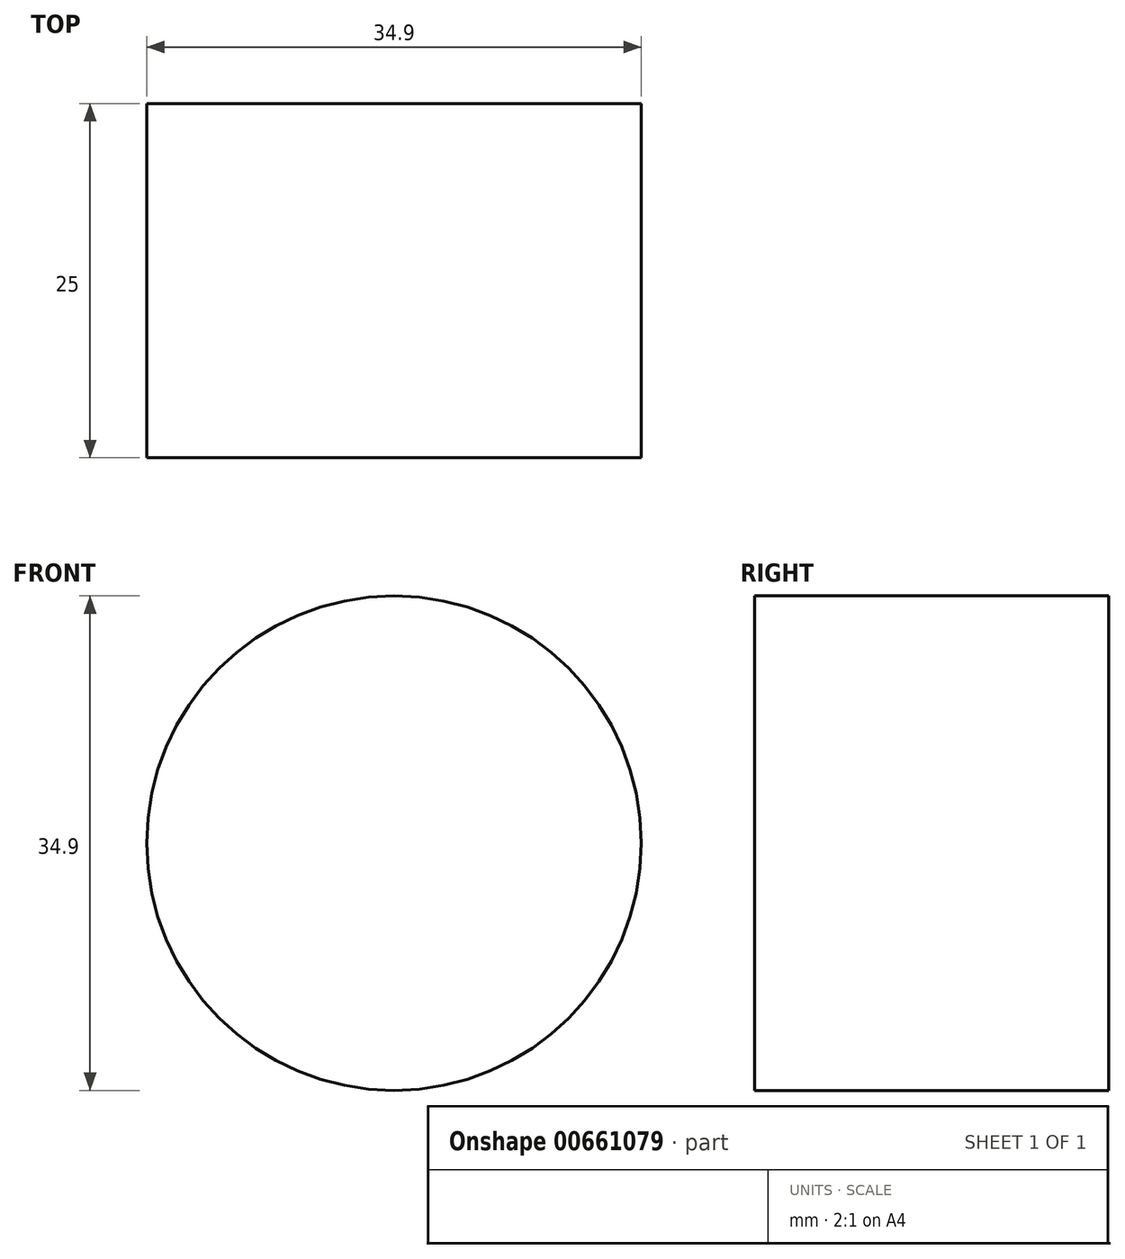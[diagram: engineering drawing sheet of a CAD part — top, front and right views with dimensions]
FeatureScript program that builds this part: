
annotation { "Feature Type Name" : "Feature", "Feature Type Description" : "" }
export const myFeature = defineFeature(function(context is Context, id is Id, definition is map)
    precondition{}
    {
        {
            var Q0;
            Q0=qCreatedBy(makeId("Front.planeOp"),FACE);
            var sketch = newSketch(context, id + "F0", { "sketchPlane" : qUnion([Q0])});
            skCircle(sketch, "E0", {"center": v(0, 0) * mm, "radius": 17.45 * mm});
            skSolve(sketch);
        }
        {
            var Q0;
            Q0=sQuery(id+"F0.wireOp",EDGE,"E0");
            extrude(context, id + "F1", {"bodyType" : ToolBodyType.SURFACE, "surfaceEntities" : qUnion([Q0]), "depth" : 25 * mm, "offsetDistance" : 25 * mm});
        }
    });
